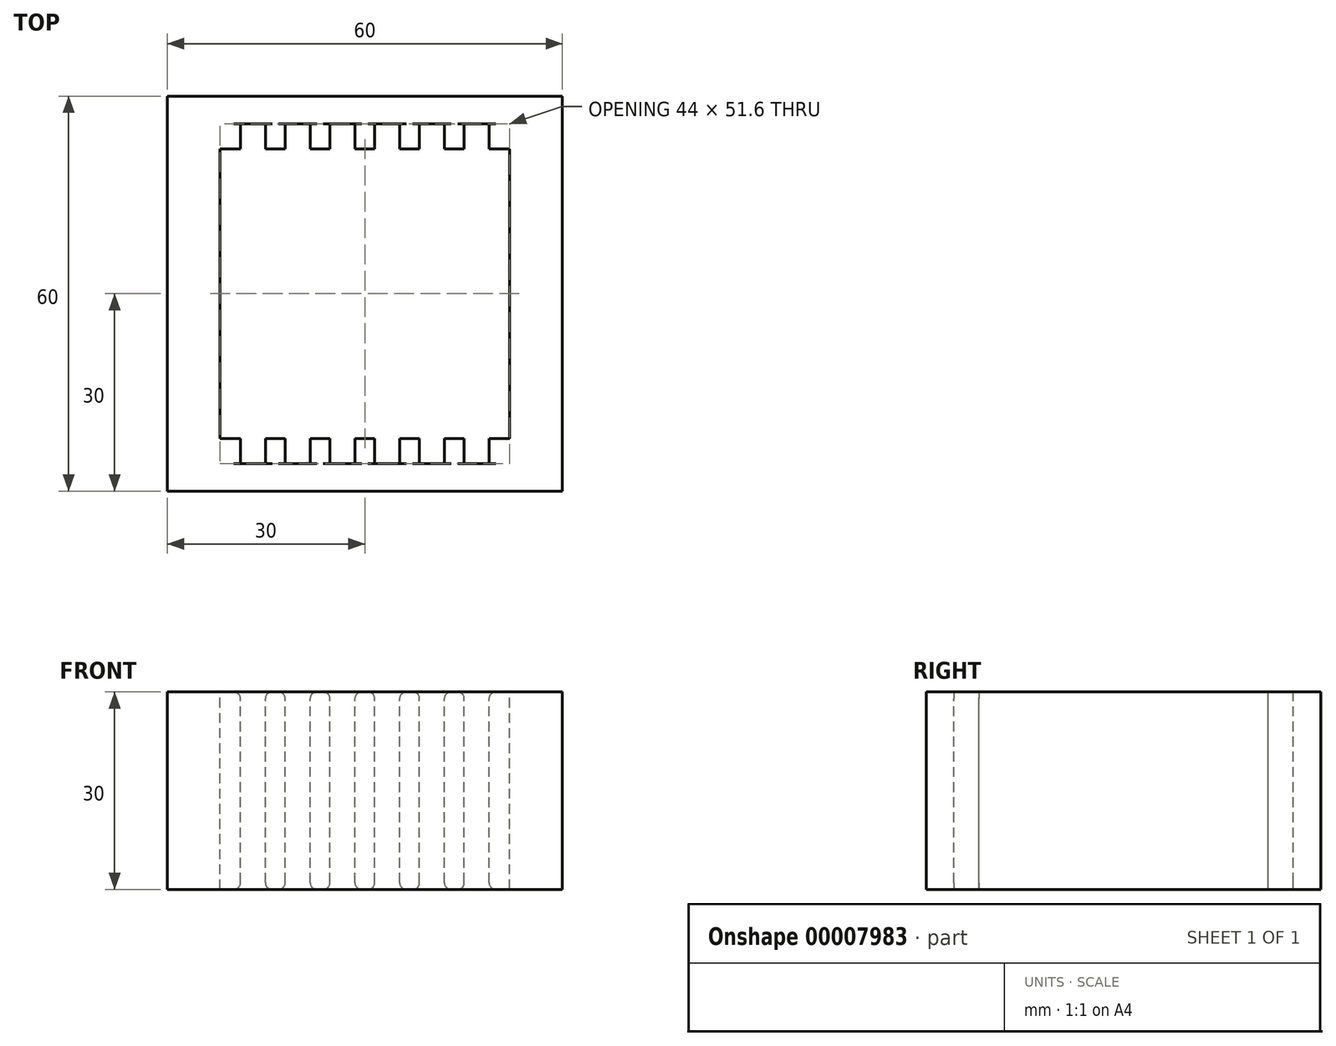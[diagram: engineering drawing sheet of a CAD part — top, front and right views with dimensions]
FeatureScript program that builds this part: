
annotation { "Feature Type Name" : "Feature", "Feature Type Description" : "" }
export const myFeature = defineFeature(function(context is Context, id is Id, definition is map)
    precondition{}
    {
        {
            var Q0;
            Q0=qCreatedBy(makeId("Top.planeOp"),FACE);
            var sketch = newSketch(context, id + "F0", { "sketchPlane" : qUnion([Q0])});
            skLineSegment(sketch, "E0.bottom", {"start": v(0, 0) * mm, "end": v(60, 0) * mm});
            skLineSegment(sketch, "E0.top", {"start": v(0, 60) * mm, "end": v(60, 60) * mm});
            skLineSegment(sketch, "E0.left", {"start": v(0, 0) * mm, "end": v(0, 60) * mm});
            skLineSegment(sketch, "E0.right", {"start": v(60, 0) * mm, "end": v(60, 60) * mm});
            skLineSegment(sketch, "E1", {"start": v(60, 30) * mm, "end": v(0, 30) * mm, "construction": true});
            skPoint(sketch, "E1.endSnap0", {"position": v(0, 30) * mm});
            skLineSegment(sketch, "E2", {"start": v(30, 60) * mm, "end": v(30, 0) * mm, "construction": true});
            skLineSegment(sketch, "E3.0", {"start": v(8, 52) * mm, "end": v(52, 52) * mm});
            skLineSegment(sketch, "E3.1", {"start": v(8, 8) * mm, "end": v(8, 52) * mm});
            skLineSegment(sketch, "E3.2", {"start": v(8, 8) * mm, "end": v(52, 8) * mm});
            skLineSegment(sketch, "E3.3", {"start": v(52, 8) * mm, "end": v(52, 52) * mm});
            skLineSegment(sketch, "E4.bottom", {"start": v(11.1, 55.8) * mm, "end": v(14.9, 55.8) * mm});
            skLineSegment(sketch, "E4.top", {"start": v(11.1, 4.2) * mm, "end": v(14.9, 4.2) * mm});
            skLineSegment(sketch, "E4.left", {"start": v(11.1, 55.8) * mm, "end": v(11.1, 4.2) * mm});
            skLineSegment(sketch, "E4.right", {"start": v(14.9, 55.8) * mm, "end": v(14.9, 4.2) * mm});
            skPoint(sketch, "E5", {"position": v(14.9, 30) * mm});
            skLineSegment(sketch, "E6.1.0.0", {"start": v(17.9, 4.2) * mm, "end": v(21.7, 4.2) * mm});
            skLineSegment(sketch, "E6.1.0.1", {"start": v(17.9, 55.8) * mm, "end": v(21.7, 55.8) * mm});
            skLineSegment(sketch, "E6.1.0.2", {"start": v(21.7, 55.8) * mm, "end": v(21.7, 4.2) * mm});
            skLineSegment(sketch, "E6.1.0.3", {"start": v(17.9, 55.8) * mm, "end": v(17.9, 4.2) * mm});
            skLineSegment(sketch, "E6.2.0.0", {"start": v(24.7, 4.2) * mm, "end": v(28.5, 4.2) * mm});
            skLineSegment(sketch, "E6.2.0.1", {"start": v(24.7, 55.8) * mm, "end": v(28.5, 55.8) * mm});
            skLineSegment(sketch, "E6.2.0.2", {"start": v(28.5, 55.8) * mm, "end": v(28.5, 4.2) * mm});
            skLineSegment(sketch, "E6.2.0.3", {"start": v(24.7, 55.8) * mm, "end": v(24.7, 4.2) * mm});
            skLineSegment(sketch, "E6.3.0.0", {"start": v(31.5, 4.2) * mm, "end": v(35.3, 4.2) * mm});
            skLineSegment(sketch, "E6.3.0.1", {"start": v(31.5, 55.8) * mm, "end": v(35.3, 55.8) * mm});
            skLineSegment(sketch, "E6.3.0.2", {"start": v(35.3, 55.8) * mm, "end": v(35.3, 4.2) * mm});
            skLineSegment(sketch, "E6.3.0.3", {"start": v(31.5, 55.8) * mm, "end": v(31.5, 4.2) * mm});
            skLineSegment(sketch, "E6.4.0.0", {"start": v(38.3, 4.2) * mm, "end": v(42.1, 4.2) * mm});
            skLineSegment(sketch, "E6.4.0.1", {"start": v(38.3, 55.8) * mm, "end": v(42.1, 55.8) * mm});
            skLineSegment(sketch, "E6.4.0.2", {"start": v(42.1, 55.8) * mm, "end": v(42.1, 4.2) * mm});
            skLineSegment(sketch, "E6.4.0.3", {"start": v(38.3, 55.8) * mm, "end": v(38.3, 4.2) * mm});
            skLineSegment(sketch, "E6.5.0.0", {"start": v(45.1, 4.2) * mm, "end": v(48.9, 4.2) * mm});
            skLineSegment(sketch, "E6.5.0.1", {"start": v(45.1, 55.8) * mm, "end": v(48.9, 55.8) * mm});
            skLineSegment(sketch, "E6.5.0.2", {"start": v(48.9, 55.8) * mm, "end": v(48.9, 4.2) * mm});
            skLineSegment(sketch, "E6.5.0.3", {"start": v(45.1, 55.8) * mm, "end": v(45.1, 4.2) * mm});
            skLineSegment(sketch, "E6.direction1", {"start": v(11.1, 4.2) * mm, "end": v(17.9, 4.2) * mm, "construction": true});
            skSolve(sketch);
        }
        {
            var Q0;
            Q0=makeQuery(id+"F0.imprint","IMPRINT",FACE,{"disambiguationData":[TD([[makeQuery(id+"F0.imprint","IMPRINT",EDGE,{"derivedFrom":sQuery(id+"F0.wireOp",EDGE,"E0.bottom")}),1.0]])]});
            extrude(context, id + "F1", {"entities" : qUnion([Q0]), "oppositeDirection" : true, "depth" : 30 * mm, "offsetDistance" : 25 * mm});
        }
        {
            var Q0;
            {var subQ0=sQuery(id+"F0.wireOp",EDGE,"E4.left");Q0=makeQuery(id+"F1.opExtrude","CAP_EDGE",EDGE,{"disambiguationData":[OSD([subQ0]),TDD([makeQuery(id+"F0.imprint","IMPRINT",EDGE,{"disambiguationData":[TD([[makeQuery(id+"F0.imprint","INTERSECT",VERTEX,{"derivedFrom":[sQuery(id+"F0.wireOp",EDGE,"E4.bottom"),subQ0]}),-1.0]])],"derivedFrom":subQ0})])],"isStart":true});}
            var Q1;
            {var subQ0=sQuery(id+"F0.wireOp",EDGE,"E4.right");Q1=makeQuery(id+"F1.opExtrude","CAP_EDGE",EDGE,{"disambiguationData":[OSD([subQ0]),TDD([makeQuery(id+"F0.imprint","IMPRINT",EDGE,{"disambiguationData":[TD([[makeQuery(id+"F0.imprint","INTERSECT",VERTEX,{"derivedFrom":[sQuery(id+"F0.wireOp",EDGE,"E4.bottom"),subQ0]}),-1.0]])],"derivedFrom":subQ0})])],"isStart":true});}
            var Q2;
            {var subQ0=sQuery(id+"F0.wireOp",EDGE,"E6.1.0.3");Q2=makeQuery(id+"F1.opExtrude","CAP_EDGE",EDGE,{"disambiguationData":[OSD([subQ0]),TDD([makeQuery(id+"F0.imprint","IMPRINT",EDGE,{"disambiguationData":[TD([[makeQuery(id+"F0.imprint","INTERSECT",VERTEX,{"derivedFrom":[sQuery(id+"F0.wireOp",EDGE,"E6.1.0.1"),subQ0]}),-1.0]])],"derivedFrom":subQ0})])],"isStart":true});}
            var Q3;
            {var subQ0=sQuery(id+"F0.wireOp",EDGE,"E6.1.0.2");Q3=makeQuery(id+"F1.opExtrude","CAP_EDGE",EDGE,{"disambiguationData":[OSD([subQ0]),TDD([makeQuery(id+"F0.imprint","IMPRINT",EDGE,{"disambiguationData":[TD([[makeQuery(id+"F0.imprint","INTERSECT",VERTEX,{"derivedFrom":[sQuery(id+"F0.wireOp",EDGE,"E6.1.0.1"),subQ0]}),-1.0]])],"derivedFrom":subQ0})])],"isStart":true});}
            var Q4;
            {var subQ0=sQuery(id+"F0.wireOp",EDGE,"E6.2.0.3");Q4=makeQuery(id+"F1.opExtrude","CAP_EDGE",EDGE,{"disambiguationData":[OSD([subQ0]),TDD([makeQuery(id+"F0.imprint","IMPRINT",EDGE,{"disambiguationData":[TD([[makeQuery(id+"F0.imprint","INTERSECT",VERTEX,{"derivedFrom":[sQuery(id+"F0.wireOp",EDGE,"E6.2.0.1"),subQ0]}),-1.0]])],"derivedFrom":subQ0})])],"isStart":true});}
            var Q5;
            {var subQ0=sQuery(id+"F0.wireOp",EDGE,"E6.2.0.2");Q5=makeQuery(id+"F1.opExtrude","CAP_EDGE",EDGE,{"disambiguationData":[OSD([subQ0]),TDD([makeQuery(id+"F0.imprint","IMPRINT",EDGE,{"disambiguationData":[TD([[makeQuery(id+"F0.imprint","INTERSECT",VERTEX,{"derivedFrom":[sQuery(id+"F0.wireOp",EDGE,"E6.2.0.1"),subQ0]}),-1.0]])],"derivedFrom":subQ0})])],"isStart":true});}
            var Q6;
            {var subQ0=sQuery(id+"F0.wireOp",EDGE,"E6.3.0.3");Q6=makeQuery(id+"F1.opExtrude","CAP_EDGE",EDGE,{"disambiguationData":[OSD([subQ0]),TDD([makeQuery(id+"F0.imprint","IMPRINT",EDGE,{"disambiguationData":[TD([[makeQuery(id+"F0.imprint","INTERSECT",VERTEX,{"derivedFrom":[sQuery(id+"F0.wireOp",EDGE,"E6.3.0.1"),subQ0]}),-1.0]])],"derivedFrom":subQ0})])],"isStart":true});}
            var Q7;
            {var subQ0=sQuery(id+"F0.wireOp",EDGE,"E6.3.0.2");Q7=makeQuery(id+"F1.opExtrude","CAP_EDGE",EDGE,{"disambiguationData":[OSD([subQ0]),TDD([makeQuery(id+"F0.imprint","IMPRINT",EDGE,{"disambiguationData":[TD([[makeQuery(id+"F0.imprint","INTERSECT",VERTEX,{"derivedFrom":[sQuery(id+"F0.wireOp",EDGE,"E6.3.0.1"),subQ0]}),-1.0]])],"derivedFrom":subQ0})])],"isStart":true});}
            var Q8;
            {var subQ0=sQuery(id+"F0.wireOp",EDGE,"E6.4.0.3");Q8=makeQuery(id+"F1.opExtrude","CAP_EDGE",EDGE,{"disambiguationData":[OSD([subQ0]),TDD([makeQuery(id+"F0.imprint","IMPRINT",EDGE,{"disambiguationData":[TD([[makeQuery(id+"F0.imprint","INTERSECT",VERTEX,{"derivedFrom":[sQuery(id+"F0.wireOp",EDGE,"E6.4.0.1"),subQ0]}),-1.0]])],"derivedFrom":subQ0})])],"isStart":true});}
            var Q9;
            {var subQ0=sQuery(id+"F0.wireOp",EDGE,"E6.4.0.2");Q9=makeQuery(id+"F1.opExtrude","CAP_EDGE",EDGE,{"disambiguationData":[OSD([subQ0]),TDD([makeQuery(id+"F0.imprint","IMPRINT",EDGE,{"disambiguationData":[TD([[makeQuery(id+"F0.imprint","INTERSECT",VERTEX,{"derivedFrom":[sQuery(id+"F0.wireOp",EDGE,"E6.4.0.1"),subQ0]}),-1.0]])],"derivedFrom":subQ0})])],"isStart":true});}
            var Q10;
            {var subQ0=sQuery(id+"F0.wireOp",EDGE,"E6.5.0.3");Q10=makeQuery(id+"F1.opExtrude","CAP_EDGE",EDGE,{"disambiguationData":[OSD([subQ0]),TDD([makeQuery(id+"F0.imprint","IMPRINT",EDGE,{"disambiguationData":[TD([[makeQuery(id+"F0.imprint","INTERSECT",VERTEX,{"derivedFrom":[sQuery(id+"F0.wireOp",EDGE,"E6.5.0.1"),subQ0]}),-1.0]])],"derivedFrom":subQ0})])],"isStart":true});}
            var Q11;
            {var subQ0=sQuery(id+"F0.wireOp",EDGE,"E6.5.0.2");Q11=makeQuery(id+"F1.opExtrude","CAP_EDGE",EDGE,{"disambiguationData":[OSD([subQ0]),TDD([makeQuery(id+"F0.imprint","IMPRINT",EDGE,{"disambiguationData":[TD([[makeQuery(id+"F0.imprint","INTERSECT",VERTEX,{"derivedFrom":[sQuery(id+"F0.wireOp",EDGE,"E6.5.0.1"),subQ0]}),-1.0]])],"derivedFrom":subQ0})])],"isStart":true});}
            var Q12;
            {var subQ0=sQuery(id+"F0.wireOp",EDGE,"E6.5.0.2");Q12=makeQuery(id+"F1.opExtrude","CAP_EDGE",EDGE,{"disambiguationData":[OSD([subQ0]),TDD([makeQuery(id+"F0.imprint","IMPRINT",EDGE,{"disambiguationData":[TD([[makeQuery(id+"F0.imprint","INTERSECT",VERTEX,{"derivedFrom":[sQuery(id+"F0.wireOp",EDGE,"E6.5.0.0"),subQ0]}),1.0]])],"derivedFrom":subQ0})])],"isStart":true});}
            var Q13;
            {var subQ0=sQuery(id+"F0.wireOp",EDGE,"E6.5.0.3");Q13=makeQuery(id+"F1.opExtrude","CAP_EDGE",EDGE,{"disambiguationData":[OSD([subQ0]),TDD([makeQuery(id+"F0.imprint","IMPRINT",EDGE,{"disambiguationData":[TD([[makeQuery(id+"F0.imprint","INTERSECT",VERTEX,{"derivedFrom":[sQuery(id+"F0.wireOp",EDGE,"E6.5.0.0"),subQ0]}),1.0]])],"derivedFrom":subQ0})])],"isStart":true});}
            var Q14;
            {var subQ0=sQuery(id+"F0.wireOp",EDGE,"E6.4.0.2");Q14=makeQuery(id+"F1.opExtrude","CAP_EDGE",EDGE,{"disambiguationData":[OSD([subQ0]),TDD([makeQuery(id+"F0.imprint","IMPRINT",EDGE,{"disambiguationData":[TD([[makeQuery(id+"F0.imprint","INTERSECT",VERTEX,{"derivedFrom":[sQuery(id+"F0.wireOp",EDGE,"E6.4.0.0"),subQ0]}),1.0]])],"derivedFrom":subQ0})])],"isStart":true});}
            var Q15;
            {var subQ0=sQuery(id+"F0.wireOp",EDGE,"E6.4.0.3");Q15=makeQuery(id+"F1.opExtrude","CAP_EDGE",EDGE,{"disambiguationData":[OSD([subQ0]),TDD([makeQuery(id+"F0.imprint","IMPRINT",EDGE,{"disambiguationData":[TD([[makeQuery(id+"F0.imprint","INTERSECT",VERTEX,{"derivedFrom":[sQuery(id+"F0.wireOp",EDGE,"E6.4.0.0"),subQ0]}),1.0]])],"derivedFrom":subQ0})])],"isStart":true});}
            var Q16;
            {var subQ0=sQuery(id+"F0.wireOp",EDGE,"E6.3.0.2");Q16=makeQuery(id+"F1.opExtrude","CAP_EDGE",EDGE,{"disambiguationData":[OSD([subQ0]),TDD([makeQuery(id+"F0.imprint","IMPRINT",EDGE,{"disambiguationData":[TD([[makeQuery(id+"F0.imprint","INTERSECT",VERTEX,{"derivedFrom":[sQuery(id+"F0.wireOp",EDGE,"E6.3.0.0"),subQ0]}),1.0]])],"derivedFrom":subQ0})])],"isStart":true});}
            var Q17;
            {var subQ0=sQuery(id+"F0.wireOp",EDGE,"E6.3.0.3");Q17=makeQuery(id+"F1.opExtrude","CAP_EDGE",EDGE,{"disambiguationData":[OSD([subQ0]),TDD([makeQuery(id+"F0.imprint","IMPRINT",EDGE,{"disambiguationData":[TD([[makeQuery(id+"F0.imprint","INTERSECT",VERTEX,{"derivedFrom":[sQuery(id+"F0.wireOp",EDGE,"E6.3.0.0"),subQ0]}),1.0]])],"derivedFrom":subQ0})])],"isStart":true});}
            var Q18;
            {var subQ0=sQuery(id+"F0.wireOp",EDGE,"E6.2.0.2");Q18=makeQuery(id+"F1.opExtrude","CAP_EDGE",EDGE,{"disambiguationData":[OSD([subQ0]),TDD([makeQuery(id+"F0.imprint","IMPRINT",EDGE,{"disambiguationData":[TD([[makeQuery(id+"F0.imprint","INTERSECT",VERTEX,{"derivedFrom":[sQuery(id+"F0.wireOp",EDGE,"E6.2.0.0"),subQ0]}),1.0]])],"derivedFrom":subQ0})])],"isStart":true});}
            var Q19;
            {var subQ0=sQuery(id+"F0.wireOp",EDGE,"E6.2.0.3");Q19=makeQuery(id+"F1.opExtrude","CAP_EDGE",EDGE,{"disambiguationData":[OSD([subQ0]),TDD([makeQuery(id+"F0.imprint","IMPRINT",EDGE,{"disambiguationData":[TD([[makeQuery(id+"F0.imprint","INTERSECT",VERTEX,{"derivedFrom":[sQuery(id+"F0.wireOp",EDGE,"E6.2.0.0"),subQ0]}),1.0]])],"derivedFrom":subQ0})])],"isStart":true});}
            var Q20;
            {var subQ0=sQuery(id+"F0.wireOp",EDGE,"E6.1.0.2");Q20=makeQuery(id+"F1.opExtrude","CAP_EDGE",EDGE,{"disambiguationData":[OSD([subQ0]),TDD([makeQuery(id+"F0.imprint","IMPRINT",EDGE,{"disambiguationData":[TD([[makeQuery(id+"F0.imprint","INTERSECT",VERTEX,{"derivedFrom":[sQuery(id+"F0.wireOp",EDGE,"E6.1.0.0"),subQ0]}),1.0]])],"derivedFrom":subQ0})])],"isStart":true});}
            var Q21;
            {var subQ0=sQuery(id+"F0.wireOp",EDGE,"E6.1.0.3");Q21=makeQuery(id+"F1.opExtrude","CAP_EDGE",EDGE,{"disambiguationData":[OSD([subQ0]),TDD([makeQuery(id+"F0.imprint","IMPRINT",EDGE,{"disambiguationData":[TD([[makeQuery(id+"F0.imprint","INTERSECT",VERTEX,{"derivedFrom":[sQuery(id+"F0.wireOp",EDGE,"E6.1.0.0"),subQ0]}),1.0]])],"derivedFrom":subQ0})])],"isStart":true});}
            var Q22;
            {var subQ0=sQuery(id+"F0.wireOp",EDGE,"E4.right");Q22=makeQuery(id+"F1.opExtrude","CAP_EDGE",EDGE,{"disambiguationData":[OSD([subQ0]),TDD([makeQuery(id+"F0.imprint","IMPRINT",EDGE,{"disambiguationData":[TD([[makeQuery(id+"F0.imprint","INTERSECT",VERTEX,{"derivedFrom":[sQuery(id+"F0.wireOp",EDGE,"E4.top"),subQ0]}),1.0]])],"derivedFrom":subQ0})])],"isStart":true});}
            var Q23;
            {var subQ0=sQuery(id+"F0.wireOp",EDGE,"E4.left");Q23=makeQuery(id+"F1.opExtrude","CAP_EDGE",EDGE,{"disambiguationData":[OSD([subQ0]),TDD([makeQuery(id+"F0.imprint","IMPRINT",EDGE,{"disambiguationData":[TD([[makeQuery(id+"F0.imprint","INTERSECT",VERTEX,{"derivedFrom":[sQuery(id+"F0.wireOp",EDGE,"E4.top"),subQ0]}),1.0]])],"derivedFrom":subQ0})])],"isStart":true});}
            var Q24;
            {var subQ0=sQuery(id+"F0.wireOp",EDGE,"E6.5.0.2");Q24=makeQuery(id+"F1.opExtrude","CAP_EDGE",EDGE,{"disambiguationData":[OSD([subQ0]),TDD([makeQuery(id+"F0.imprint","IMPRINT",EDGE,{"disambiguationData":[TD([[makeQuery(id+"F0.imprint","INTERSECT",VERTEX,{"derivedFrom":[sQuery(id+"F0.wireOp",EDGE,"E6.5.0.1"),subQ0]}),-1.0]])],"derivedFrom":subQ0})])],"isStart":false});}
            var Q25;
            {var subQ0=sQuery(id+"F0.wireOp",EDGE,"E6.5.0.3");Q25=makeQuery(id+"F1.opExtrude","CAP_EDGE",EDGE,{"disambiguationData":[OSD([subQ0]),TDD([makeQuery(id+"F0.imprint","IMPRINT",EDGE,{"disambiguationData":[TD([[makeQuery(id+"F0.imprint","INTERSECT",VERTEX,{"derivedFrom":[sQuery(id+"F0.wireOp",EDGE,"E6.5.0.1"),subQ0]}),-1.0]])],"derivedFrom":subQ0})])],"isStart":false});}
            var Q26;
            {var subQ0=sQuery(id+"F0.wireOp",EDGE,"E6.4.0.3");Q26=makeQuery(id+"F1.opExtrude","CAP_EDGE",EDGE,{"disambiguationData":[OSD([subQ0]),TDD([makeQuery(id+"F0.imprint","IMPRINT",EDGE,{"disambiguationData":[TD([[makeQuery(id+"F0.imprint","INTERSECT",VERTEX,{"derivedFrom":[sQuery(id+"F0.wireOp",EDGE,"E6.4.0.1"),subQ0]}),-1.0]])],"derivedFrom":subQ0})])],"isStart":false});}
            var Q27;
            {var subQ0=sQuery(id+"F0.wireOp",EDGE,"E6.3.0.3");Q27=makeQuery(id+"F1.opExtrude","CAP_EDGE",EDGE,{"disambiguationData":[OSD([subQ0]),TDD([makeQuery(id+"F0.imprint","IMPRINT",EDGE,{"disambiguationData":[TD([[makeQuery(id+"F0.imprint","INTERSECT",VERTEX,{"derivedFrom":[sQuery(id+"F0.wireOp",EDGE,"E6.3.0.1"),subQ0]}),-1.0]])],"derivedFrom":subQ0})])],"isStart":false});}
            var Q28;
            {var subQ0=sQuery(id+"F0.wireOp",EDGE,"E6.2.0.3");Q28=makeQuery(id+"F1.opExtrude","CAP_EDGE",EDGE,{"disambiguationData":[OSD([subQ0]),TDD([makeQuery(id+"F0.imprint","IMPRINT",EDGE,{"disambiguationData":[TD([[makeQuery(id+"F0.imprint","INTERSECT",VERTEX,{"derivedFrom":[sQuery(id+"F0.wireOp",EDGE,"E6.2.0.1"),subQ0]}),-1.0]])],"derivedFrom":subQ0})])],"isStart":false});}
            var Q29;
            {var subQ0=sQuery(id+"F0.wireOp",EDGE,"E6.1.0.3");Q29=makeQuery(id+"F1.opExtrude","CAP_EDGE",EDGE,{"disambiguationData":[OSD([subQ0]),TDD([makeQuery(id+"F0.imprint","IMPRINT",EDGE,{"disambiguationData":[TD([[makeQuery(id+"F0.imprint","INTERSECT",VERTEX,{"derivedFrom":[sQuery(id+"F0.wireOp",EDGE,"E6.1.0.1"),subQ0]}),-1.0]])],"derivedFrom":subQ0})])],"isStart":false});}
            var Q30;
            {var subQ0=sQuery(id+"F0.wireOp",EDGE,"E4.left");Q30=makeQuery(id+"F1.opExtrude","CAP_EDGE",EDGE,{"disambiguationData":[OSD([subQ0]),TDD([makeQuery(id+"F0.imprint","IMPRINT",EDGE,{"disambiguationData":[TD([[makeQuery(id+"F0.imprint","INTERSECT",VERTEX,{"derivedFrom":[sQuery(id+"F0.wireOp",EDGE,"E4.bottom"),subQ0]}),-1.0]])],"derivedFrom":subQ0})])],"isStart":false});}
            var Q31;
            {var subQ0=sQuery(id+"F0.wireOp",EDGE,"E6.1.0.2");Q31=makeQuery(id+"F1.opExtrude","CAP_EDGE",EDGE,{"disambiguationData":[OSD([subQ0]),TDD([makeQuery(id+"F0.imprint","IMPRINT",EDGE,{"disambiguationData":[TD([[makeQuery(id+"F0.imprint","INTERSECT",VERTEX,{"derivedFrom":[sQuery(id+"F0.wireOp",EDGE,"E6.1.0.1"),subQ0]}),-1.0]])],"derivedFrom":subQ0})])],"isStart":false});}
            var Q32;
            {var subQ0=sQuery(id+"F0.wireOp",EDGE,"E6.4.0.2");Q32=makeQuery(id+"F1.opExtrude","CAP_EDGE",EDGE,{"disambiguationData":[OSD([subQ0]),TDD([makeQuery(id+"F0.imprint","IMPRINT",EDGE,{"disambiguationData":[TD([[makeQuery(id+"F0.imprint","INTERSECT",VERTEX,{"derivedFrom":[sQuery(id+"F0.wireOp",EDGE,"E6.4.0.1"),subQ0]}),-1.0]])],"derivedFrom":subQ0})])],"isStart":false});}
            var Q33;
            {var subQ0=sQuery(id+"F0.wireOp",EDGE,"E6.3.0.2");Q33=makeQuery(id+"F1.opExtrude","CAP_EDGE",EDGE,{"disambiguationData":[OSD([subQ0]),TDD([makeQuery(id+"F0.imprint","IMPRINT",EDGE,{"disambiguationData":[TD([[makeQuery(id+"F0.imprint","INTERSECT",VERTEX,{"derivedFrom":[sQuery(id+"F0.wireOp",EDGE,"E6.3.0.1"),subQ0]}),-1.0]])],"derivedFrom":subQ0})])],"isStart":false});}
            var Q34;
            {var subQ0=sQuery(id+"F0.wireOp",EDGE,"E4.right");Q34=makeQuery(id+"F1.opExtrude","CAP_EDGE",EDGE,{"disambiguationData":[OSD([subQ0]),TDD([makeQuery(id+"F0.imprint","IMPRINT",EDGE,{"disambiguationData":[TD([[makeQuery(id+"F0.imprint","INTERSECT",VERTEX,{"derivedFrom":[sQuery(id+"F0.wireOp",EDGE,"E4.bottom"),subQ0]}),-1.0]])],"derivedFrom":subQ0})])],"isStart":false});}
            var Q35;
            {var subQ0=sQuery(id+"F0.wireOp",EDGE,"E6.2.0.2");Q35=makeQuery(id+"F1.opExtrude","CAP_EDGE",EDGE,{"disambiguationData":[OSD([subQ0]),TDD([makeQuery(id+"F0.imprint","IMPRINT",EDGE,{"disambiguationData":[TD([[makeQuery(id+"F0.imprint","INTERSECT",VERTEX,{"derivedFrom":[sQuery(id+"F0.wireOp",EDGE,"E6.2.0.1"),subQ0]}),-1.0]])],"derivedFrom":subQ0})])],"isStart":false});}
            var Q36;
            {var subQ0=sQuery(id+"F0.wireOp",EDGE,"E4.left");Q36=makeQuery(id+"F1.opExtrude","CAP_EDGE",EDGE,{"disambiguationData":[OSD([subQ0]),TDD([makeQuery(id+"F0.imprint","IMPRINT",EDGE,{"disambiguationData":[TD([[makeQuery(id+"F0.imprint","INTERSECT",VERTEX,{"derivedFrom":[sQuery(id+"F0.wireOp",EDGE,"E4.top"),subQ0]}),1.0]])],"derivedFrom":subQ0})])],"isStart":false});}
            var Q37;
            {var subQ0=sQuery(id+"F0.wireOp",EDGE,"E4.right");Q37=makeQuery(id+"F1.opExtrude","CAP_EDGE",EDGE,{"disambiguationData":[OSD([subQ0]),TDD([makeQuery(id+"F0.imprint","IMPRINT",EDGE,{"disambiguationData":[TD([[makeQuery(id+"F0.imprint","INTERSECT",VERTEX,{"derivedFrom":[sQuery(id+"F0.wireOp",EDGE,"E4.top"),subQ0]}),1.0]])],"derivedFrom":subQ0})])],"isStart":false});}
            var Q38;
            {var subQ0=sQuery(id+"F0.wireOp",EDGE,"E6.1.0.2");Q38=makeQuery(id+"F1.opExtrude","CAP_EDGE",EDGE,{"disambiguationData":[OSD([subQ0]),TDD([makeQuery(id+"F0.imprint","IMPRINT",EDGE,{"disambiguationData":[TD([[makeQuery(id+"F0.imprint","INTERSECT",VERTEX,{"derivedFrom":[sQuery(id+"F0.wireOp",EDGE,"E6.1.0.0"),subQ0]}),1.0]])],"derivedFrom":subQ0})])],"isStart":false});}
            var Q39;
            {var subQ0=sQuery(id+"F0.wireOp",EDGE,"E6.2.0.3");Q39=makeQuery(id+"F1.opExtrude","CAP_EDGE",EDGE,{"disambiguationData":[OSD([subQ0]),TDD([makeQuery(id+"F0.imprint","IMPRINT",EDGE,{"disambiguationData":[TD([[makeQuery(id+"F0.imprint","INTERSECT",VERTEX,{"derivedFrom":[sQuery(id+"F0.wireOp",EDGE,"E6.2.0.0"),subQ0]}),1.0]])],"derivedFrom":subQ0})])],"isStart":false});}
            var Q40;
            {var subQ0=sQuery(id+"F0.wireOp",EDGE,"E6.2.0.2");Q40=makeQuery(id+"F1.opExtrude","CAP_EDGE",EDGE,{"disambiguationData":[OSD([subQ0]),TDD([makeQuery(id+"F0.imprint","IMPRINT",EDGE,{"disambiguationData":[TD([[makeQuery(id+"F0.imprint","INTERSECT",VERTEX,{"derivedFrom":[sQuery(id+"F0.wireOp",EDGE,"E6.2.0.0"),subQ0]}),1.0]])],"derivedFrom":subQ0})])],"isStart":false});}
            var Q41;
            {var subQ0=sQuery(id+"F0.wireOp",EDGE,"E6.3.0.3");Q41=makeQuery(id+"F1.opExtrude","CAP_EDGE",EDGE,{"disambiguationData":[OSD([subQ0]),TDD([makeQuery(id+"F0.imprint","IMPRINT",EDGE,{"disambiguationData":[TD([[makeQuery(id+"F0.imprint","INTERSECT",VERTEX,{"derivedFrom":[sQuery(id+"F0.wireOp",EDGE,"E6.3.0.0"),subQ0]}),1.0]])],"derivedFrom":subQ0})])],"isStart":false});}
            var Q42;
            {var subQ0=sQuery(id+"F0.wireOp",EDGE,"E6.3.0.2");Q42=makeQuery(id+"F1.opExtrude","CAP_EDGE",EDGE,{"disambiguationData":[OSD([subQ0]),TDD([makeQuery(id+"F0.imprint","IMPRINT",EDGE,{"disambiguationData":[TD([[makeQuery(id+"F0.imprint","INTERSECT",VERTEX,{"derivedFrom":[sQuery(id+"F0.wireOp",EDGE,"E6.3.0.0"),subQ0]}),1.0]])],"derivedFrom":subQ0})])],"isStart":false});}
            var Q43;
            {var subQ0=sQuery(id+"F0.wireOp",EDGE,"E6.4.0.3");Q43=makeQuery(id+"F1.opExtrude","CAP_EDGE",EDGE,{"disambiguationData":[OSD([subQ0]),TDD([makeQuery(id+"F0.imprint","IMPRINT",EDGE,{"disambiguationData":[TD([[makeQuery(id+"F0.imprint","INTERSECT",VERTEX,{"derivedFrom":[sQuery(id+"F0.wireOp",EDGE,"E6.4.0.0"),subQ0]}),1.0]])],"derivedFrom":subQ0})])],"isStart":false});}
            var Q44;
            {var subQ0=sQuery(id+"F0.wireOp",EDGE,"E6.4.0.2");Q44=makeQuery(id+"F1.opExtrude","CAP_EDGE",EDGE,{"disambiguationData":[OSD([subQ0]),TDD([makeQuery(id+"F0.imprint","IMPRINT",EDGE,{"disambiguationData":[TD([[makeQuery(id+"F0.imprint","INTERSECT",VERTEX,{"derivedFrom":[sQuery(id+"F0.wireOp",EDGE,"E6.4.0.0"),subQ0]}),1.0]])],"derivedFrom":subQ0})])],"isStart":false});}
            var Q45;
            {var subQ0=sQuery(id+"F0.wireOp",EDGE,"E6.5.0.3");Q45=makeQuery(id+"F1.opExtrude","CAP_EDGE",EDGE,{"disambiguationData":[OSD([subQ0]),TDD([makeQuery(id+"F0.imprint","IMPRINT",EDGE,{"disambiguationData":[TD([[makeQuery(id+"F0.imprint","INTERSECT",VERTEX,{"derivedFrom":[sQuery(id+"F0.wireOp",EDGE,"E6.5.0.0"),subQ0]}),1.0]])],"derivedFrom":subQ0})])],"isStart":false});}
            var Q46;
            {var subQ0=sQuery(id+"F0.wireOp",EDGE,"E6.5.0.2");Q46=makeQuery(id+"F1.opExtrude","CAP_EDGE",EDGE,{"disambiguationData":[OSD([subQ0]),TDD([makeQuery(id+"F0.imprint","IMPRINT",EDGE,{"disambiguationData":[TD([[makeQuery(id+"F0.imprint","INTERSECT",VERTEX,{"derivedFrom":[sQuery(id+"F0.wireOp",EDGE,"E6.5.0.0"),subQ0]}),1.0]])],"derivedFrom":subQ0})])],"isStart":false});}
            var Q47;
            {var subQ0=sQuery(id+"F0.wireOp",EDGE,"E6.1.0.3");Q47=makeQuery(id+"F1.opExtrude","CAP_EDGE",EDGE,{"disambiguationData":[OSD([subQ0]),TDD([makeQuery(id+"F0.imprint","IMPRINT",EDGE,{"disambiguationData":[TD([[makeQuery(id+"F0.imprint","INTERSECT",VERTEX,{"derivedFrom":[sQuery(id+"F0.wireOp",EDGE,"E6.1.0.0"),subQ0]}),1.0]])],"derivedFrom":subQ0})])],"isStart":false});}
            fillet(context, id + "F2", {"entities" : qUnion([Q0, Q1, Q2, Q3, Q4, Q5, Q6, Q7, Q8, Q9, Q10, Q11, Q12, Q13, Q14, Q15, Q16, Q17, Q18, Q19, Q20, Q21, Q22, Q23, Q24, Q25, Q26, Q27, Q28, Q29, Q30, Q31, Q32, Q33, Q34, Q35, Q36, Q37, Q38, Q39, Q40, Q41, Q42, Q43, Q44, Q45, Q46, Q47]), "radius" : 1 * mm, "tangentPropagation" : true, "allowEdgeOverflow" : false});
        }
    });
